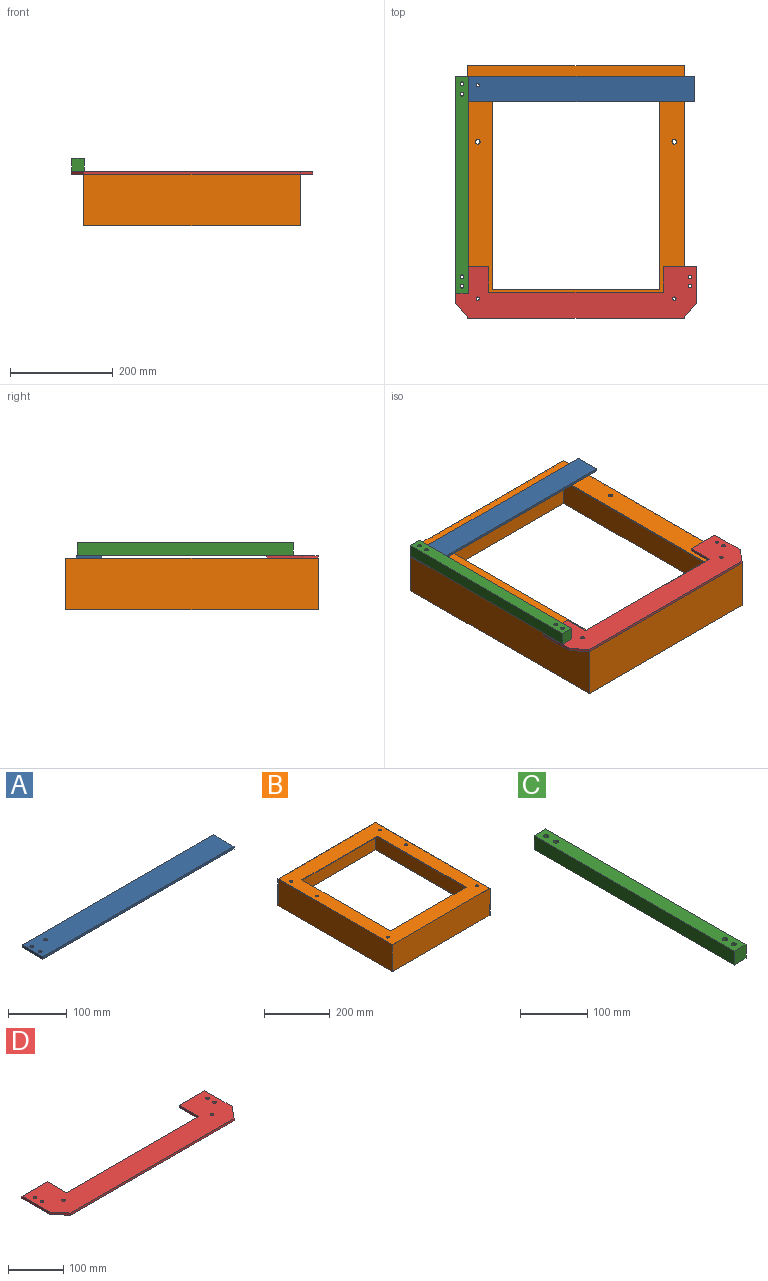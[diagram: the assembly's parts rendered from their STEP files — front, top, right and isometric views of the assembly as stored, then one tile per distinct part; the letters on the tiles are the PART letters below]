
ASSEMBLY  parts=4 mates=4
PART A: 9 faces, bbox 460x50x5 mm
  f0: plane 460x5mm, normal (0,1,0), area 2300mm2, adj f1,f6,f7,f8
  f1: plane 50x5mm, normal (-1,0,0), area 250mm2, adj f0,f2,f7,f8
  f2: plane 460x5mm, normal (0,-1,0), area 2300mm2, adj f1,f6,f7,f8
  f3: cylinder r=3.35mm len=6.7mm, axis (0,0,-1), area 105.2mm2, adj f7,f8
  f4: cylinder r=3.35mm len=6.7mm, axis (0,0,-1), area 105.2mm2, adj f7,f8
  f5: cylinder r=3.35mm len=6.7mm, axis (0,0,-1), area 105.2mm2, adj f7,f8
  f6: plane 50x5mm, normal (1,0,0), area 250mm2, adj f0,f2,f7,f8
  f7: plane 460x50mm, normal (0,0,1), area 22894.2mm2, adj f0,f1,f2,f3,f4,f5,f6
  f8: plane 460x50mm, normal (0,0,-1), area 22894.2mm2, adj f0,f1,f2,f3,f4,f5,f6
PART B: 21 faces, bbox 420x490x100 mm
  f0: plane 490x420mm, normal (0,0,1), area 81918.3mm2, adj f3,f4,f5,f6,f11,f12,f13,f14
  f1: plane 486x416mm, normal (0,0,-1), area 78294.3mm2, adj f7,f8,f9,f10,f11,f12,f13,f14
  f2: plane 490x420mm, normal (0,0,-1), area 3624mm2, adj f3,f4,f5,f6,f7,f8,f9,f10
  f3: plane 420x100mm, normal (0,1,0), area 42000mm2, adj f0,f2,f4,f6
  f4: plane 490x100mm, normal (-1,0,0), area 49000mm2, adj f0,f2,f3,f5
  f5: plane 420x100mm, normal (0,-1,0), area 42000mm2, adj f0,f2,f4,f6
  f6: plane 490x100mm, normal (1,0,0), area 49000mm2, adj f0,f2,f3,f5
  f7: plane 416x98mm, normal (0,-1,0), area 40768mm2, adj f1,f2,f8,f10
  f8: plane 486x98mm, normal (1,0,0), area 47628mm2, adj f1,f2,f7,f9
  f9: plane 416x98mm, normal (0,1,0), area 40768mm2, adj f1,f2,f8,f10
  f10: plane 486x98mm, normal (-1,0,0), area 47628mm2, adj f1,f2,f7,f9
  f11: plane 325x2mm, normal (0,-1,0), area 650mm2, adj f0,f1,f12,f14
  f12: plane 380x2mm, normal (1,0,0), area 760mm2, adj f0,f1,f11,f13
  f13: plane 325x2mm, normal (0,1,0), area 650mm2, adj f0,f1,f12,f14
  f14: plane 380x2mm, normal (-1,0,0), area 760mm2, adj f0,f1,f11,f13
  f15: cylinder r=4.5mm len=9mm, axis (0,0,1), area 56.5mm2, adj f0,f1
  f16: cylinder r=4.5mm len=9mm, axis (0,0,1), area 56.5mm2, adj f0,f1
  f17: cylinder r=4.5mm len=9mm, axis (0,0,1), area 56.5mm2, adj f0,f1
  f18: cylinder r=4.5mm len=9mm, axis (0,0,1), area 56.5mm2, adj f0,f1
  f19: cylinder r=4.5mm len=9mm, axis (0,0,1), area 56.5mm2, adj f0,f1
  f20: cylinder r=4.5mm len=9mm, axis (0,0,1), area 56.5mm2, adj f0,f1
PART C: 10 faces, bbox 25x420x25 mm
  f0: plane 25x25mm, normal (0,1,0), area 625mm2, adj f1,f3,f4,f5
  f1: plane 420x25mm, normal (-1,0,0), area 10500mm2, adj f0,f2,f4,f5
  f2: plane 25x25mm, normal (0,-1,0), area 625mm2, adj f1,f3,f4,f5
  f3: plane 420x25mm, normal (1,0,0), area 10500mm2, adj f0,f2,f4,f5
  f4: plane 420x25mm, normal (0,0,1), area 10324.2mm2, adj f0,f1,f2,f3,f6,f7,f8,f9
  f5: plane 420x25mm, normal (0,0,-1), area 10324.2mm2, adj f0,f1,f2,f3,f6,f7,f8,f9
  f6: cylinder r=3.74mm len=25mm, axis (0,0,-1), area 587.5mm2, adj f4,f5
  f7: cylinder r=3.74mm len=25mm, axis (0,0,-1), area 587.5mm2, adj f4,f5
  f8: cylinder r=3.74mm len=25mm, axis (0,0,-1), area 587.5mm2, adj f4,f5
  f9: cylinder r=3.74mm len=25mm, axis (0,0,-1), area 587.5mm2, adj f4,f5
PART D: 18 faces, bbox 470x100x5 mm
  f0: plane 30x25mm, normal (-0.77,-0.64,0), area 195.3mm2, adj f1,f14,f16,f17
  f1: plane 420x5mm, normal (0,-1,0), area 2100mm2, adj f0,f2,f16,f17
  f2: plane 30x25mm, normal (0.77,-0.64,0), area 195.3mm2, adj f1,f3,f16,f17
  f3: plane 70x5mm, normal (1,0,0), area 350mm2, adj f2,f4,f16,f17
  f4: plane 65x5mm, normal (0,1,0), area 325mm2, adj f3,f5,f16,f17
  f5: plane 50x5mm, normal (-1,0,0), area 250mm2, adj f4,f6,f16,f17
  f6: plane 340x5mm, normal (0,1,0), area 1700mm2, adj f5,f7,f16,f17
  f7: plane 50x5mm, normal (1,0,0), area 250mm2, adj f6,f8,f16,f17
  f8: plane 65x5mm, normal (0,1,0), area 325mm2, adj f7,f14,f16,f17
  f9: cylinder r=3.35mm len=6.7mm, axis (0,0,-1), area 105.2mm2, adj f16,f17
  f10: cylinder r=3.35mm len=6.7mm, axis (0,0,-1), area 105.2mm2, adj f16,f17
  f11: cylinder r=3.35mm len=6.7mm, axis (0,0,-1), area 105.2mm2, adj f16,f17
  f12: cylinder r=3.35mm len=6.7mm, axis (0,0,-1), area 105.2mm2, adj f16,f17
  f13: cylinder r=3.35mm len=6.7mm, axis (0,0,-1), area 105.2mm2, adj f16,f17
  f14: plane 70x5mm, normal (-1,0,0), area 350mm2, adj f0,f8,f16,f17
  f15: cylinder r=3.35mm len=6.7mm, axis (0,0,-1), area 105.2mm2, adj f16,f17
  f16: plane 470x100mm, normal (0,0,1), area 29038.5mm2, adj f0,f1,f2,f3,f4,f5,f6,f7
  f17: plane 470x100mm, normal (0,0,-1), area 29038.5mm2, adj f0,f1,f2,f3,f4,f5,f6,f7
PLACE A t=(0,445.12,0)mm
PLACE B t=(0,245,0)mm
PLACE C t=(0,237.5,-19.53)mm
PLACE D at identity
MATE parallel C.f1 <-> B.f4  axis (-1,0,0) through (-234,258.5,17.97)mm
MATE planar B.f0 <-> D.f17  axis (0,0,1) through (0,0,0)mm
MATE cylindrical A.f3 <-> C.f9  axis (0,0,1) through (-221.5,455,5)mm
MATE cylindrical C.f7 <-> D.f11  axis (0,0,1) through (-221.5,62,30.47)mm
